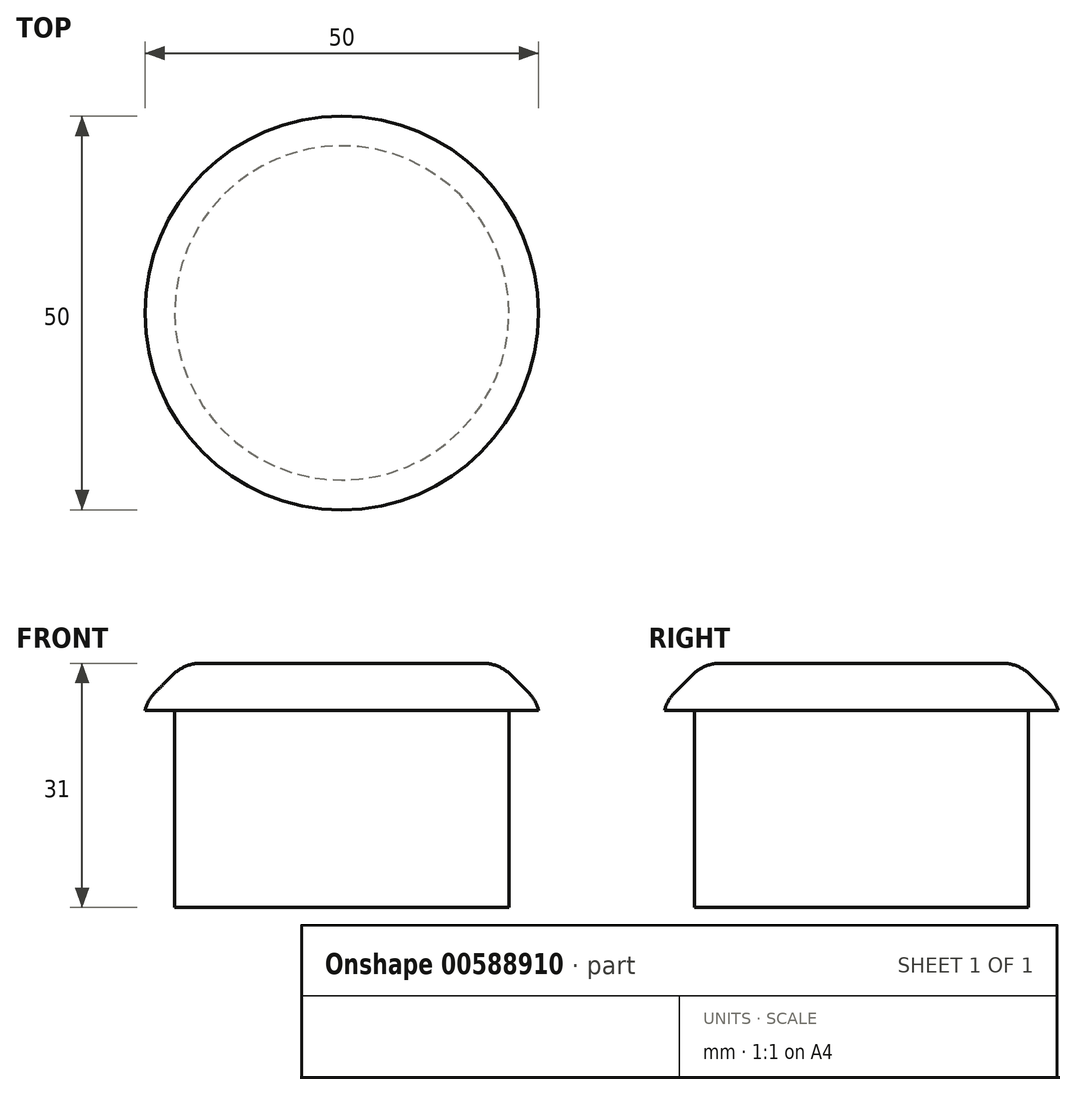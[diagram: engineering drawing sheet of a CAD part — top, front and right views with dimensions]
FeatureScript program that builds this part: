
annotation { "Feature Type Name" : "Feature", "Feature Type Description" : "" }
export const myFeature = defineFeature(function(context is Context, id is Id, definition is map)
    precondition{}
    {
        {
            var Q0;
            Q0=qCreatedBy(makeId("Top.planeOp"),FACE);
            var sketch = newSketch(context, id + "F0", { "sketchPlane" : qUnion([Q0])});
            skCircle(sketch, "E0", {"center": v(0, 0) * mm, "radius": 25 * mm});
            skSolve(sketch);
        }
        {
            var Q0;
            Q0 = qSketchRegion(id + "F0", true);
            extrude(context, id + "F1", {"entities" : qUnion([Q0]), "depth" : 6 * mm, "offsetDistance" : 25 * mm});
        }
        {
            var Q0;
            Q0=makeQuery(id+"F1.opExtrude","CAP_FACE",FACE,{"disambiguationData":[OSD([sQuery(id+"F0.wireOp",EDGE,"E0")])],"isStart":false});
            var sketch = newSketch(context, id + "F2", { "sketchPlane" : qUnion([Q0])});
            skCircle(sketch, "E1", {"center": v(0, 0) * mm, "radius": 21.43 * mm});
            skSolve(sketch);
        }
        {
            var Q0;
            Q0 = qSketchRegion(id + "F2", true);
            extrude(context, id + "F3", {"entities" : qUnion([Q0]), "operationType" : NewBodyOperationType.ADD, "depth" : -3 * mm, "offsetDistance" : 25 * mm});
        }
        {
            var Q0;
            Q0=makeQuery(id+"F1.opExtrude","CAP_EDGE",EDGE,{"disambiguationData":[OSD([sQuery(id+"F0.wireOp",EDGE,"E0")])],"isStart":false});
            chamfer(context, id + "F4", {"entities" : qUnion([Q0]), "width" : 5 * mm, "tangentPropagation" : true});
        }
        {
            var Q0;
            Q0=makeQuery(id+"F4.opChamfer","BLEND_FACE",FACE,{"disambiguationData":[OSD([sQuery(id+"F0.wireOp",EDGE,"E0")])]});
            fillet(context, id + "F5", {"entities" : qUnion([Q0]), "radius" : 5 * mm, "tangentPropagation" : true, "allowEdgeOverflow" : false});
        }
        {
            var Q0;
            Q0=makeQuery(id+"F1.opExtrude","CAP_FACE",FACE,{"disambiguationData":[OSD([sQuery(id+"F0.wireOp",EDGE,"E0")])],"isStart":true});
            var sketch = newSketch(context, id + "F6", { "sketchPlane" : qUnion([Q0])});
            skCircle(sketch, "E2", {"center": v(0, 0) * mm, "radius": 21.84 * mm});
            skSolve(sketch);
        }
        {
            var Q0;
            Q0 = qSketchRegion(id + "F6", true);
            extrude(context, id + "F7", {"entities" : qUnion([Q0]), "operationType" : NewBodyOperationType.ADD, "depth" : -4 * mm, "offsetDistance" : 25 * mm});
        }
        {
            var Q0;
            Q0=makeQuery(id+"F1.opExtrude","CAP_FACE",FACE,{"disambiguationData":[OSD([sQuery(id+"F0.wireOp",EDGE,"E0")])],"isStart":true});
            var sketch = newSketch(context, id + "F8", { "sketchPlane" : qUnion([Q0])});
            skCircle(sketch, "E3", {"center": v(0, 0) * mm, "radius": 21.23 * mm});
            skSolve(sketch);
        }
        {
            var Q0;
            Q0 = qSketchRegion(id + "F8", true);
            extrude(context, id + "F9", {"entities" : qUnion([Q0]), "operationType" : NewBodyOperationType.ADD, "depth" : 25 * mm, "offsetDistance" : 25 * mm});
        }
    });
